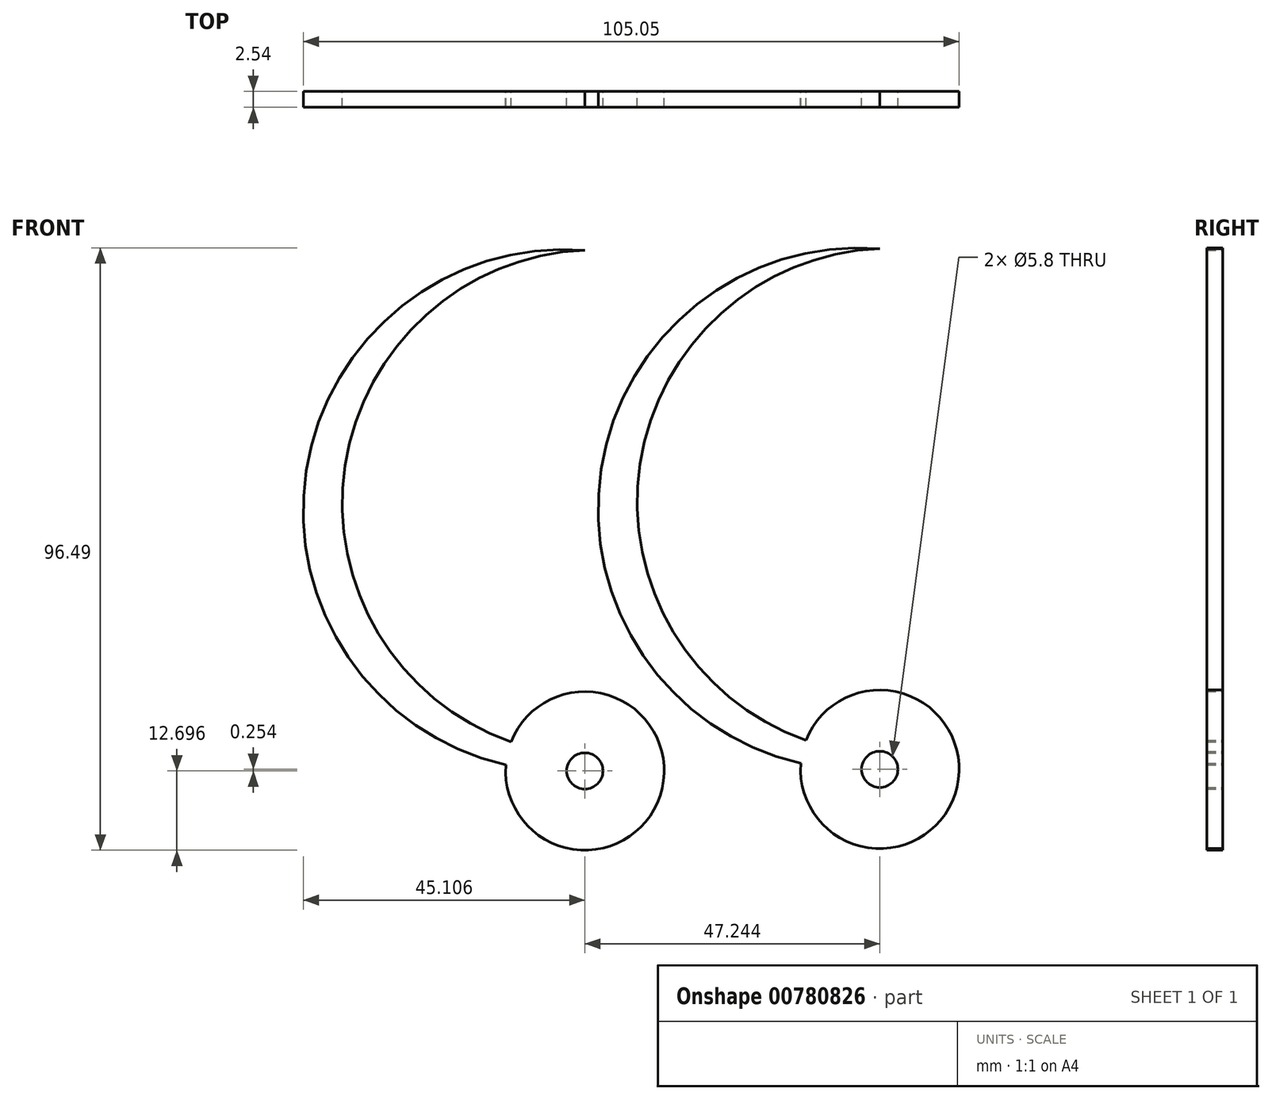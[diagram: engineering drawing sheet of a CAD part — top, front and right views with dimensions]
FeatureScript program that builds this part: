
annotation { "Feature Type Name" : "Feature", "Feature Type Description" : "" }
export const myFeature = defineFeature(function(context is Context, id is Id, definition is map)
    precondition{}
    {
        {
            var Q0;
            Q0=qCreatedBy(makeId("Front.planeOp"),FACE);
            var sketch = newSketch(context, id + "F0", { "sketchPlane" : qUnion([Q0])});
            skArc(sketch, "E0", {"start": v(0, 83.41) * mm, "mid": v(-44.62, 48.06) * mm, "end": v(-12.67, 0.94) * mm});
            skPoint(sketch, "E0.first.point", {"position": v(0, 0) * mm});
            skPoint(sketch, "E0.second.point", {"position": v(-45.09, 43.05) * mm});
            skPoint(sketch, "E0.third.point", {"position": v(0, 83.41) * mm});
            skArc(sketch, "E1", {"start": v(-12.67, 0.94) * mm, "mid": v(12.38, -2.82) * mm, "end": v(-11.82, 4.64) * mm});
            skArc(sketch, "E2", {"start": v(0, 83.41) * mm, "mid": v(-38.4, 48.9) * mm, "end": v(-11.82, 4.64) * mm});
            skPoint(sketch, "E2.first.point", {"position": v(12.16, 3.68) * mm});
            skPoint(sketch, "E2.second.point", {"position": v(-38.84, 41.7) * mm});
            skCircle(sketch, "E3", {"center": v(0, 0) * mm, "radius": 2.9 * mm});
            skSolve(sketch);
        }
        {
            var Q0;
            Q0 = qSketchRegion(id + "F0", true);
            extrude(context, id + "F1", {"entities" : qUnion([Q0]), "depth" : 2.54 * mm, "offsetDistance" : 25.4 * mm});
        }
        {
            var Q0;
            Q0=makeQuery(id+"F1.opExtrude","SWEPT_BODY",BODY,{"disambiguationData":[OSD([sQuery(id+"F0.wireOp",EDGE,"E0"),sQuery(id+"F0.wireOp",EDGE,"E1"),sQuery(id+"F0.wireOp",EDGE,"E2")])]});
            transform(context, id + "F2", {"entities" : qUnion([Q0]), "transformType" : TransformType.TRANSLATION_3D, "dx" : -47.24 * mm, "dy" : 0 * mm, "dz" : -0.25 * mm, "makeCopy" : true});
        }
    });
